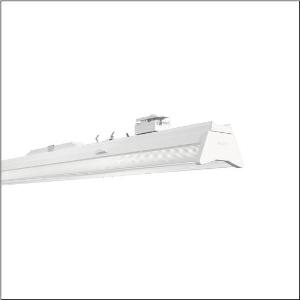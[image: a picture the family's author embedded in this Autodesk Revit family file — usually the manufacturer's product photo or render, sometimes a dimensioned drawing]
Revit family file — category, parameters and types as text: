
# Revit family: licross_11_performance_mo_51tm16dn445g
name_source: partatom
category: Lighting Fixtures
units: mm (PartAtom-declared; Revit-internal decimal feet)

## family parameters
Cut with Voids When Loaded = No
Host = Face
Light Source = No
Part Type = Normal
Room Calculation Point = No
Round Connector Dimension = Use Diameter
Shared = No

## types (1)
- --- (1 x LED, 4520 lm, 24.3 W, 4000K)
    Apparent Load = 24 VA
    CIE Flux Codes = 66 88 96 79 100
    Color Rendering = 80
    Color Temperature = 4000K
    Default Elevation = 1800 mm
    Description = Licross 11 Performance MO, luminaire insert, of sheet steel, galvanised, coil coated, white, length: 1.500mm, width: 120mm, height: 123mm, LED rated luminous flux: 4.520lm, light colour: 840, SDCM (Standard Deviation of Colour Matching)MacAdam ≤ 2 SDCM (initial), control gear: DALI 2, with plug, 5-pole, with phase selection, mains connection: 220..240V, AC, 50/60Hz, rated input power: 24W, internal wiring halogen-free, primary light control with lens, of plastic, primary optical cover: cover, of PMMA, CAT 2 (L<= 3000cd/m²), light emission: direct/indirect distribution, primary light characteristic: symmetric, protection rating (complete): IP40, insulation class (complete): insulation class I (protective earthing), certification: CE, ENEC, VDE, UKCA, protection symbol: D if used in an environment without relevant dust loads with corresponding accessories, impact resistance: IK06, permissible ambient temperature for indoor applications: -25..+45°C, corresponds to IFS (International Featured Standards) requirements for safety and quality in the food industry, reducing of maximum allowable ambient temperature of 5°C with ceiling mounting, LABS conformity tested according to VDMA 24364:2018-05, The light source and the operating device comply with the requirements of the Ecodesign Regulation (EU) 2019/2020 and are replaceable in accordance with this regulation, packaging unit: 1 piece
    Height = 114 mm
    Lamp = 1 x LED
    Lamp Light Flux = 4520 lm
    Lamp Power = 24.3 W
    Lamp count = 1
    Length = 1500 mm
    Luminous efficacy = 186 lm/W
    Manufacturer = Siteco
    ModVariant = No
    Model = 51TM16DN445G
    Mounting Place = Ceiling
    Mounting Type = Pendant
    Number of Poles = 1
    OnlyDefault = Yes
    Power Factor = 1
    Product Name = Licross 11 Performance MO
    Product group = luminaire insert | ceiling pendant
    ProductGroupID = 901
    Protection Class = Protection class I
    Protection Degree = IP 40
    RLX_Detail_Level = 1
    RLX_Emergency_Light_Flux = 0 lm
    RLX_Emergency_Type = 0
    RLX_Emergency_Type_DB = No
    RlxData = <blob elided: 34013 chars, md5=27423c8b>
    Socket = socket
    Standby Power = 0 W
    System Light Flux = 4520 lm
    System Power = 24 W
    Type Comments = factory setting: luminous flux: 100 % | dim-lin: 254 | 161 mA
    Type Image = l_1256138.jpg
    URL = http://relux.com
    VarID = @adj_057883
    Voltage = 0 V
    Weight = 0.00 kg
    Width = 120 mm

## geometry (parser evidence)
native form markers: Blend x4, Sweep x10
no freeform markers — native parametric forms only
